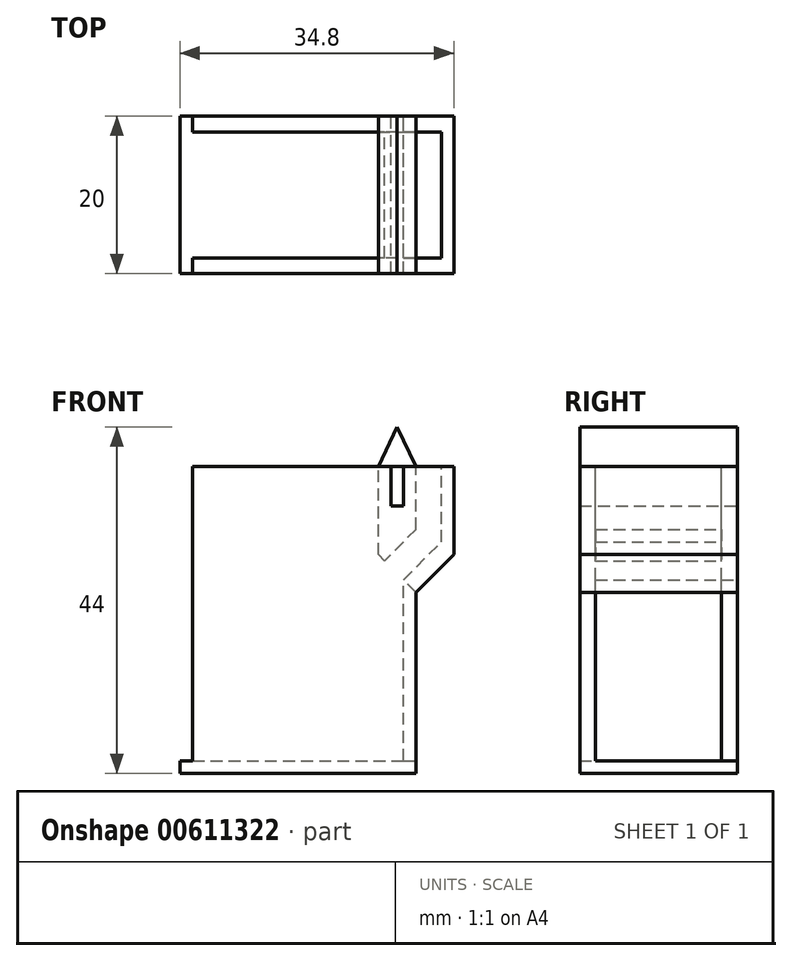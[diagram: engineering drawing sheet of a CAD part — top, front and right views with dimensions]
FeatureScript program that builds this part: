
annotation { "Feature Type Name" : "Feature", "Feature Type Description" : "" }
export const myFeature = defineFeature(function(context is Context, id is Id, definition is map)
    precondition{}
    {
        {
            var Q0;
            Q0=qCreatedBy(makeId("Front.planeOp"),FACE);
            var sketch = newSketch(context, id + "F0", { "sketchPlane" : qUnion([Q0])});
            skLineSegment(sketch, "E0.bottom", {"start": v(-12.76, 1.6) * mm, "end": v(17.24, 1.6) * mm});
            skLineSegment(sketch, "E0.top", {"start": v(-12.76, 0) * mm, "end": v(17.24, 0) * mm});
            skLineSegment(sketch, "E0.left", {"start": v(-12.76, 1.6) * mm, "end": v(-12.76, 0) * mm});
            skLineSegment(sketch, "E0.right", {"start": v(17.24, 1.6) * mm, "end": v(17.24, 0) * mm});
            skLineSegment(sketch, "E1.bottom", {"start": v(17.24, 1.6) * mm, "end": v(14.04, 1.6) * mm});
            skLineSegment(sketch, "E1.top", {"start": v(17.24, 39) * mm, "end": v(12.44, 39) * mm});
            skLineSegment(sketch, "E1.left", {"start": v(17.24, 1.6) * mm, "end": v(17.24, 23) * mm});
            skLineSegment(sketch, "E2", {"start": v(12.44, 39) * mm, "end": v(14.84, 44) * mm});
            skLineSegment(sketch, "E3", {"start": v(14.84, 44) * mm, "end": v(17.24, 39) * mm});
            skLineSegment(sketch, "E4", {"start": v(-11.16, 39) * mm, "end": v(12.44, 39) * mm});
            skLineSegment(sketch, "E5.bottom", {"start": v(14.04, 39) * mm, "end": v(15.64, 39) * mm});
            skLineSegment(sketch, "E5.top", {"start": v(14.04, 34) * mm, "end": v(15.64, 34) * mm});
            skLineSegment(sketch, "E5.left", {"start": v(14.04, 39) * mm, "end": v(14.04, 34) * mm});
            skLineSegment(sketch, "E5.right", {"start": v(15.64, 39) * mm, "end": v(15.64, 34) * mm});
            skPoint(sketch, "E6", {"position": v(14.84, 39) * mm});
            skLineSegment(sketch, "E7.bottom", {"start": v(-12.76, 1.6) * mm, "end": v(-11.16, 1.6) * mm});
            skLineSegment(sketch, "E7.top", {"start": v(-12.76, 39) * mm, "end": v(-11.16, 39) * mm});
            skLineSegment(sketch, "E7.left", {"start": v(-12.76, 1.6) * mm, "end": v(-12.76, 39) * mm});
            skLineSegment(sketch, "E7.right", {"start": v(-11.16, 1.6) * mm, "end": v(-11.16, 39) * mm});
            skLineSegment(sketch, "E8", {"start": v(17.24, 23) * mm, "end": v(12.44, 27.8) * mm});
            skLineSegment(sketch, "E9", {"start": v(12.44, 27.8) * mm, "end": v(12.44, 39) * mm});
            skLineSegment(sketch, "E10", {"start": v(17.24, 23) * mm, "end": v(17.24, 39) * mm});
            skLineSegment(sketch, "E11", {"start": v(15.64, 1.6) * mm, "end": v(15.64, 24.6) * mm});
            skLineSegment(sketch, "E12", {"start": v(17.24, 23) * mm, "end": v(22.04, 27.8) * mm});
            skLineSegment(sketch, "E13", {"start": v(22.04, 27.8) * mm, "end": v(22.04, 39) * mm});
            skLineSegment(sketch, "E14", {"start": v(22.04, 39) * mm, "end": v(17.24, 39) * mm});
            skLineSegment(sketch, "E15", {"start": v(15.64, 24.6) * mm, "end": v(20.44, 29.4) * mm});
            skLineSegment(sketch, "E16", {"start": v(20.44, 29.4) * mm, "end": v(20.44, 39) * mm});
            skLineSegment(sketch, "E17", {"start": v(17.24, 31) * mm, "end": v(13.24, 27) * mm});
            skPoint(sketch, "E17.endSnap0", {"position": v(18.04, 27) * mm});
            skSolve(sketch);
        }
        {
            var Q0;
            {var subQ1=sQuery(id+"F0.wireOp",EDGE,"E1.bottom");Q0=makeQuery(id+"F0.imprint","IMPRINT",FACE,{"disambiguationData":[TD([[makeQuery(id+"F0.imprint","IMPRINT",EDGE,{"derivedFrom":subQ1}),-1.0]])]});}
            var Q1;
            Q1=makeQuery(id+"F0.imprint","IMPRINT",FACE,{"disambiguationData":[TD([[makeQuery(id+"F0.imprint","IMPRINT",EDGE,{"derivedFrom":sQuery(id+"F0.wireOp",EDGE,"E0.top")}),1.0]])]});
            var Q2;
            Q2=makeQuery(id+"F0.imprint","IMPRINT",FACE,{"disambiguationData":[TD([[makeQuery(id+"F0.imprint","IMPRINT",EDGE,{"derivedFrom":sQuery(id+"F0.wireOp",EDGE,"E7.bottom")}),1.0]])]});
            var Q3;
            {var subQ1=sQuery(id+"F0.wireOp",EDGE,"E12");Q3=makeQuery(id+"F0.imprint","IMPRINT",FACE,{"disambiguationData":[TD([[makeQuery(id+"F0.imprint","IMPRINT",EDGE,{"derivedFrom":subQ1}),1.0]])]});}
            var Q4;
            {var subQ0=sQuery(id+"F0.wireOp",EDGE,"E10");var subQ3=sQuery(id+"F0.wireOp",EDGE,"E15");var subQ5=makeQuery(id+"F0.imprint","INTERSECT",VERTEX,{"derivedFrom":[subQ0,subQ3]});Q4=makeQuery(id+"F0.imprint","IMPRINT",FACE,{"disambiguationData":[TD([[makeQuery(id+"F0.imprint","IMPRINT",EDGE,{"disambiguationData":[TD([[subQ5,1.0]])],"derivedFrom":subQ3}),-1.0]])]});}
            var Q5;
            Q5=makeQuery(id+"F0.imprint","IMPRINT",FACE,{"disambiguationData":[TD([[makeQuery(id+"F0.imprint","IMPRINT",EDGE,{"derivedFrom":sQuery(id+"F0.wireOp",EDGE,"E5.top")}),-1.0]])]});
            extrude(context, id + "F1", {"entities" : qUnion([Q0, Q1, Q2, Q3, Q4, Q5]), "depth" : 20 * mm, "offsetDistance" : 25 * mm});
        }
        {
            var Q0;
            {var subQ5=sQuery(id+"F0.wireOp",EDGE,"E16");Q0=makeQuery(id+"F0.imprint","IMPRINT",FACE,{"disambiguationData":[TD([[makeQuery(id+"F0.imprint","IMPRINT",EDGE,{"derivedFrom":subQ5}),1.0]])]});}
            var Q1;
            Q1=makeQuery(id+"F0.imprint","IMPRINT",FACE,{"disambiguationData":[TD([[makeQuery(id+"F0.imprint","IMPRINT",EDGE,{"derivedFrom":sQuery(id+"F0.wireOp",EDGE,"E5.top")}),-1.0]])]});
            var Q2;
            {var subQ0=sQuery(id+"F0.wireOp",EDGE,"E0.bottom");Q2=makeQuery(id+"F0.imprint","IMPRINT",FACE,{"disambiguationData":[TD([[makeQuery(id+"F0.imprint","IMPRINT",EDGE,{"derivedFrom":subQ0}),1.0]])]});}
            var Q3;
            {var subQ3=sQuery(id+"F0.wireOp",EDGE,"E17");Q3=makeQuery(id+"F0.imprint","IMPRINT",FACE,{"disambiguationData":[TD([[makeQuery(id+"F0.imprint","IMPRINT",EDGE,{"derivedFrom":subQ3}),1.0]])]});}
            extrude(context, id + "F2", {"entities" : qUnion([Q0, Q1, Q2, Q3]), "operationType" : NewBodyOperationType.ADD, "depth" : 2 * mm, "offsetDistance" : 25 * mm});
        }
        {
            var Q0;
            {var subQ3=sQuery(id+"F0.wireOp",EDGE,"E17");Q0=makeQuery(id+"F0.imprint","IMPRINT",FACE,{"disambiguationData":[TD([[makeQuery(id+"F0.imprint","IMPRINT",EDGE,{"derivedFrom":subQ3}),1.0]])]});}
            var Q1;
            {var subQ3=sQuery(id+"F0.wireOp",EDGE,"E12");Q1=makeQuery(id+"F0.imprint","IMPRINT",FACE,{"disambiguationData":[TD([[makeQuery(id+"F0.imprint","IMPRINT",EDGE,{"derivedFrom":subQ3}),1.0]])]});}
            var Q2;
            {var subQ0=sQuery(id+"F0.wireOp",EDGE,"E16");Q2=makeQuery(id+"F0.imprint","IMPRINT",FACE,{"disambiguationData":[TD([[makeQuery(id+"F0.imprint","IMPRINT",EDGE,{"derivedFrom":subQ0}),1.0]])]});}
            var Q3;
            {var subQ0=sQuery(id+"F0.wireOp",EDGE,"E10");var subQ3=sQuery(id+"F0.wireOp",EDGE,"E15");var subQ5=makeQuery(id+"F0.imprint","INTERSECT",VERTEX,{"derivedFrom":[subQ0,subQ3]});Q3=makeQuery(id+"F0.imprint","IMPRINT",FACE,{"disambiguationData":[TD([[makeQuery(id+"F0.imprint","IMPRINT",EDGE,{"disambiguationData":[TD([[subQ5,1.0]])],"derivedFrom":subQ3}),-1.0]])]});}
            var Q4;
            {var subQ0=sQuery(id+"F0.wireOp",EDGE,"E1.left");Q4=makeQuery(id+"F0.imprint","IMPRINT",FACE,{"disambiguationData":[TD([[makeQuery(id+"F0.imprint","IMPRINT",EDGE,{"derivedFrom":subQ0}),1.0]])]});}
            var Q5;
            {var subQ0=sQuery(id+"F0.wireOp",EDGE,"E0.bottom");Q5=makeQuery(id+"F0.imprint","IMPRINT",FACE,{"disambiguationData":[TD([[makeQuery(id+"F0.imprint","IMPRINT",EDGE,{"derivedFrom":subQ0}),1.0]])]});}
            var Q6;
            {var subQ1=sQuery(id+"F0.wireOp",EDGE,"E0.bottom");Q6=makeQuery(id+"F0.imprint","IMPRINT",FACE,{"disambiguationData":[TD([[makeQuery(id+"F0.imprint","IMPRINT",EDGE,{"derivedFrom":subQ1}),-1.0]])]});}
            var Q7;
            Q7=makeQuery(id+"F0.imprint","IMPRINT",FACE,{"disambiguationData":[TD([[makeQuery(id+"F0.imprint","IMPRINT",EDGE,{"derivedFrom":sQuery(id+"F0.wireOp",EDGE,"E7.bottom")}),1.0]])]});
            var Q8;
            Q8=makeQuery(id+"F0.imprint","IMPRINT",FACE,{"disambiguationData":[TD([[makeQuery(id+"F0.imprint","IMPRINT",EDGE,{"derivedFrom":sQuery(id+"F0.wireOp",EDGE,"E5.top")}),-1.0]])]});
            extrude(context, id + "F3", {"entities" : qUnion([Q0, Q1, Q2, Q3, Q4, Q5, Q6, Q7, Q8]), "operationType" : NewBodyOperationType.ADD, "depth" : 20 * mm, "offsetDistance" : 25 * mm, "hasSecondDirection" : true, "secondDirectionOppositeDirection" : false, "secondDirectionDepth" : 18 * mm});
        }
        {
            var Q0;
            {var subQ1=sQuery(id+"F0.wireOp",EDGE,"E2");Q0=makeQuery(id+"F0.imprint","IMPRINT",FACE,{"disambiguationData":[TD([[makeQuery(id+"F0.imprint","IMPRINT",EDGE,{"derivedFrom":subQ1}),-1.0]])]});}
            var Q1;
            Q1=makeQuery(id+"F0.imprint","IMPRINT",FACE,{"disambiguationData":[TD([[makeQuery(id+"F0.imprint","IMPRINT",EDGE,{"derivedFrom":sQuery(id+"F0.wireOp",EDGE,"E5.bottom")}),-1.0]])]});
            var Q2;
            Q2=makeQuery(id+"F1.opExtrude","SWEPT_BODY",BODY,{"disambiguationData":[OSD([sQuery(id+"F0.wireOp",EDGE,"E0.bottom"),sQuery(id+"F0.wireOp",EDGE,"E0.top"),sQuery(id+"F0.wireOp",EDGE,"E0.left"),sQuery(id+"F0.wireOp",EDGE,"E0.right"),sQuery(id+"F0.wireOp",EDGE,"E1.top"),sQuery(id+"F0.wireOp",EDGE,"E1.left"),sQuery(id+"F0.wireOp",EDGE,"E1.right"),sQuery(id+"F0.wireOp",EDGE,"E5.top"),sQuery(id+"F0.wireOp",EDGE,"E5.left"),sQuery(id+"F0.wireOp",EDGE,"E5.right")])]});
            extrude(context, id + "F4", {"entities" : qUnion([Q0, Q1]), "depth" : 20 * mm, "endBoundEntityBody" : qUnion([Q2]), "offsetDistance" : 25 * mm});
        }
    });
